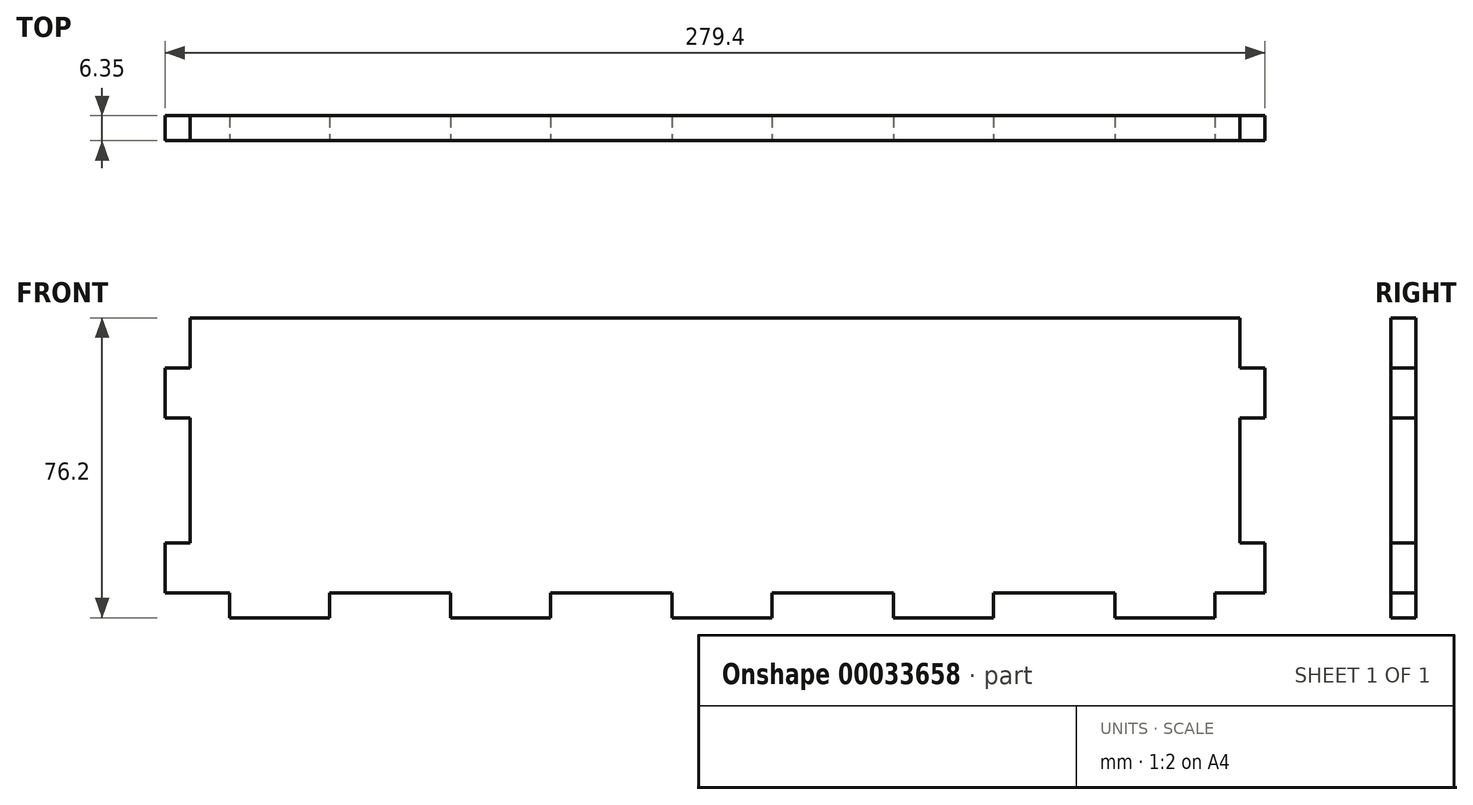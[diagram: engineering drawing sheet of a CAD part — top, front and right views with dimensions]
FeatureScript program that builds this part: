
annotation { "Feature Type Name" : "Feature", "Feature Type Description" : "" }
export const myFeature = defineFeature(function(context is Context, id is Id, definition is map)
    precondition{}
    {
        {
            var Q0;
            Q0=qCreatedBy(makeId("Front.planeOp"),FACE);
            var sketch = newSketch(context, id + "F0", { "sketchPlane" : qUnion([Q0])});
            skLineSegment(sketch, "E0.bottom", {"start": v(0, 0) * mm, "end": v(444.5, 0) * mm});
            skLineSegment(sketch, "E0.top", {"start": v(0, 76.2) * mm, "end": v(444.5, 76.2) * mm});
            skLineSegment(sketch, "E0.left", {"start": v(0, 0) * mm, "end": v(0, 76.2) * mm});
            skLineSegment(sketch, "E0.right", {"start": v(444.5, 0) * mm, "end": v(444.5, 76.2) * mm});
            skSolve(sketch);
        }
        {
            var Q0;
            Q0=makeQuery(id+"F0.imprint","IMPRINT",FACE,{"disambiguationData":[TD([[makeQuery(id+"F0.imprint","IMPRINT",EDGE,{"derivedFrom":sQuery(id+"F0.wireOp",EDGE,"E0.bottom")}),1.0]])]});
            extrude(context, id + "F1", {"entities" : qUnion([Q0]), "depth" : 6.35 * mm});
        }
        {
            var Q0;
            Q0=makeQuery(id+"F1.opExtrude","CAP_FACE",FACE,{"disambiguationData":[OSD([sQuery(id+"F0.wireOp",EDGE,"E0.bottom"),sQuery(id+"F0.wireOp",EDGE,"E0.top"),sQuery(id+"F0.wireOp",EDGE,"E0.left"),sQuery(id+"F0.wireOp",EDGE,"E0.right")])],"isStart":false});
            var sketch = newSketch(context, id + "F2", { "sketchPlane" : qUnion([Q0])});
            skLineSegment(sketch, "E1", {"start": v(222.25, 76.2) * mm, "end": v(222.25, 0) * mm, "construction": true});
            skLineSegment(sketch, "E2.bottom", {"start": v(0, 0) * mm, "end": v(6.35, 0) * mm});
            skLineSegment(sketch, "E2.top", {"start": v(0, 6.35) * mm, "end": v(6.35, 6.35) * mm});
            skLineSegment(sketch, "E2.left", {"start": v(0, 0) * mm, "end": v(0, 6.35) * mm});
            skLineSegment(sketch, "E2.right", {"start": v(6.35, 0) * mm, "end": v(6.35, 6.35) * mm});
            skLineSegment(sketch, "E3.bottom", {"start": v(0, 76.2) * mm, "end": v(6.35, 76.2) * mm});
            skLineSegment(sketch, "E3.top", {"start": v(0, 63.5) * mm, "end": v(6.35, 63.5) * mm});
            skLineSegment(sketch, "E3.left", {"start": v(0, 76.2) * mm, "end": v(0, 63.5) * mm});
            skLineSegment(sketch, "E3.right", {"start": v(6.35, 76.2) * mm, "end": v(6.35, 63.5) * mm});
            skLineSegment(sketch, "E4.bottom", {"start": v(0, 19.05) * mm, "end": v(6.35, 19.05) * mm});
            skLineSegment(sketch, "E4.top", {"start": v(0, 50.8) * mm, "end": v(6.35, 50.8) * mm});
            skLineSegment(sketch, "E4.left", {"start": v(0, 19.05) * mm, "end": v(0, 50.8) * mm});
            skLineSegment(sketch, "E4.right", {"start": v(6.35, 19.05) * mm, "end": v(6.35, 50.8) * mm});
            skLineSegment(sketch, "E5.MirrorCS", {"start": v(444.5, 6.35) * mm, "end": v(438.15, 6.35) * mm});
            skLineSegment(sketch, "E6.MirrorCS", {"start": v(444.5, 19.05) * mm, "end": v(438.15, 19.05) * mm});
            skLineSegment(sketch, "E7.MirrorCS", {"start": v(444.5, 50.8) * mm, "end": v(438.15, 50.8) * mm});
            skLineSegment(sketch, "E8.MirrorCS", {"start": v(444.5, 0) * mm, "end": v(438.15, 0) * mm});
            skLineSegment(sketch, "E9.MirrorCS", {"start": v(438.15, 76.2) * mm, "end": v(438.15, 63.5) * mm});
            skLineSegment(sketch, "E10.MirrorCS", {"start": v(438.15, 0) * mm, "end": v(438.15, 6.35) * mm});
            skLineSegment(sketch, "E11.MirrorCS", {"start": v(444.5, 0) * mm, "end": v(444.5, 6.35) * mm});
            skLineSegment(sketch, "E12.MirrorCS", {"start": v(444.5, 63.5) * mm, "end": v(438.15, 63.5) * mm});
            skLineSegment(sketch, "E13.MirrorCS", {"start": v(444.5, 76.2) * mm, "end": v(438.15, 76.2) * mm});
            skLineSegment(sketch, "E14.MirrorCS", {"start": v(444.5, 76.2) * mm, "end": v(444.5, 63.5) * mm});
            skLineSegment(sketch, "E15.MirrorCS", {"start": v(438.15, 19.05) * mm, "end": v(438.15, 50.8) * mm});
            skLineSegment(sketch, "E16.MirrorCS", {"start": v(444.5, 19.05) * mm, "end": v(444.5, 50.8) * mm});
            skSolve(sketch);
        }
        {
            var Q0;
            Q0=qSketchRegion(id+"F2",true);
            extrude(context, id + "F3", {"entities" : qUnion([Q0]), "operationType" : NewBodyOperationType.REMOVE, "endBound" : BoundingType.UP_TO_NEXT, "oppositeDirection" : true, "depth" : 25.4 * mm});
        }
        {
            var Q0;
            Q0=makeQuery(id+"F1.opExtrude","CAP_FACE",FACE,{"disambiguationData":[OSD([sQuery(id+"F0.wireOp",EDGE,"E0.bottom"),sQuery(id+"F0.wireOp",EDGE,"E0.top"),sQuery(id+"F0.wireOp",EDGE,"E0.left"),sQuery(id+"F0.wireOp",EDGE,"E0.right")])],"isStart":false});
            var sketch = newSketch(context, id + "F4", { "sketchPlane" : qUnion([Q0])});
            skLineSegment(sketch, "E17.bottom", {"start": v(38.1, 0) * mm, "end": v(68.94, 0) * mm});
            skLineSegment(sketch, "E17.top", {"start": v(38.1, 6.35) * mm, "end": v(68.94, 6.35) * mm});
            skLineSegment(sketch, "E17.left", {"start": v(38.1, 0) * mm, "end": v(38.1, 6.35) * mm});
            skLineSegment(sketch, "E17.right", {"start": v(68.94, 0) * mm, "end": v(68.94, 6.35) * mm});
            skLineSegment(sketch, "E18.1.0.0", {"start": v(125.19, 0) * mm, "end": v(125.19, 6.35) * mm});
            skLineSegment(sketch, "E18.1.0.1", {"start": v(94.34, 0) * mm, "end": v(94.34, 6.35) * mm});
            skLineSegment(sketch, "E18.1.0.2", {"start": v(94.34, 6.35) * mm, "end": v(125.19, 6.35) * mm});
            skLineSegment(sketch, "E18.1.0.3", {"start": v(94.34, 0) * mm, "end": v(125.19, 0) * mm});
            skLineSegment(sketch, "E18.2.0.0", {"start": v(181.43, 0) * mm, "end": v(181.43, 6.35) * mm});
            skLineSegment(sketch, "E18.2.0.1", {"start": v(150.59, 0) * mm, "end": v(150.59, 6.35) * mm});
            skLineSegment(sketch, "E18.2.0.2", {"start": v(150.59, 6.35) * mm, "end": v(181.43, 6.35) * mm});
            skLineSegment(sketch, "E18.2.0.3", {"start": v(150.59, 0) * mm, "end": v(181.43, 0) * mm});
            skLineSegment(sketch, "E18.3.0.0", {"start": v(237.67, 0) * mm, "end": v(237.67, 6.35) * mm});
            skLineSegment(sketch, "E18.3.0.1", {"start": v(206.83, 0) * mm, "end": v(206.83, 6.35) * mm});
            skLineSegment(sketch, "E18.3.0.2", {"start": v(206.83, 6.35) * mm, "end": v(237.67, 6.35) * mm});
            skLineSegment(sketch, "E18.3.0.3", {"start": v(206.83, 0) * mm, "end": v(237.67, 0) * mm});
            skLineSegment(sketch, "E18.4.0.0", {"start": v(293.91, 0) * mm, "end": v(293.91, 6.35) * mm});
            skLineSegment(sketch, "E18.4.0.1", {"start": v(263.07, 0) * mm, "end": v(263.07, 6.35) * mm});
            skLineSegment(sketch, "E18.4.0.2", {"start": v(263.07, 6.35) * mm, "end": v(293.91, 6.35) * mm});
            skLineSegment(sketch, "E18.4.0.3", {"start": v(263.07, 0) * mm, "end": v(293.91, 0) * mm});
            skLineSegment(sketch, "E18.direction1", {"start": v(68.94, 0) * mm, "end": v(125.19, 0) * mm, "construction": true});
            skLineSegment(sketch, "E19.0.5.0", {"start": v(350.16, 0) * mm, "end": v(350.16, 6.35) * mm});
            skLineSegment(sketch, "E19.3.5.0", {"start": v(319.31, 0) * mm, "end": v(319.31, 6.35) * mm});
            skLineSegment(sketch, "E19.6.5.0", {"start": v(319.31, 6.35) * mm, "end": v(350.16, 6.35) * mm});
            skLineSegment(sketch, "E19.9.5.0", {"start": v(319.31, 0) * mm, "end": v(350.16, 0) * mm});
            skLineSegment(sketch, "E19.0.6.0", {"start": v(406.4, 0) * mm, "end": v(406.4, 6.35) * mm});
            skLineSegment(sketch, "E19.3.6.0", {"start": v(375.56, 0) * mm, "end": v(375.56, 6.35) * mm});
            skLineSegment(sketch, "E19.6.6.0", {"start": v(375.56, 6.35) * mm, "end": v(406.4, 6.35) * mm});
            skLineSegment(sketch, "E19.9.6.0", {"start": v(375.56, 0) * mm, "end": v(406.4, 0) * mm});
            skLineSegment(sketch, "E20.bottom", {"start": v(6.35, 6.35) * mm, "end": v(12.7, 6.35) * mm});
            skLineSegment(sketch, "E20.top", {"start": v(6.35, 0) * mm, "end": v(12.7, 0) * mm});
            skLineSegment(sketch, "E20.left", {"start": v(6.35, 6.35) * mm, "end": v(6.35, 0) * mm});
            skLineSegment(sketch, "E20.right", {"start": v(12.7, 6.35) * mm, "end": v(12.7, 0) * mm});
            skLineSegment(sketch, "E21.bottom", {"start": v(438.15, 6.35) * mm, "end": v(431.8, 6.35) * mm});
            skLineSegment(sketch, "E21.top", {"start": v(438.15, 0) * mm, "end": v(431.8, 0) * mm});
            skLineSegment(sketch, "E21.left", {"start": v(438.15, 6.35) * mm, "end": v(438.15, 0) * mm});
            skLineSegment(sketch, "E21.right", {"start": v(431.8, 6.35) * mm, "end": v(431.8, 0) * mm});
            skSolve(sketch);
        }
        {
            var Q0;
            Q0=qSketchRegion(id+"F4",true);
            extrude(context, id + "F5", {"entities" : qUnion([Q0]), "operationType" : NewBodyOperationType.REMOVE, "endBound" : BoundingType.THROUGH_ALL, "oppositeDirection" : true, "depth" : 25.4 * mm});
        }
        {
            var Q0;
            Q0=makeQuery(id+"F1.opExtrude","CAP_FACE",FACE,{"disambiguationData":[OSD([sQuery(id+"F0.wireOp",EDGE,"E0.bottom"),sQuery(id+"F0.wireOp",EDGE,"E0.top"),sQuery(id+"F0.wireOp",EDGE,"E0.left"),sQuery(id+"F0.wireOp",EDGE,"E0.right")])],"isStart":false});
            var sketch = newSketch(context, id + "F6", { "sketchPlane" : qUnion([Q0])});
            skLineSegment(sketch, "E22.bottom", {"start": v(165.1, 76.2) * mm, "end": v(0, 76.2) * mm});
            skLineSegment(sketch, "E22.top", {"start": v(165.1, 0) * mm, "end": v(0, 0) * mm});
            skLineSegment(sketch, "E22.left", {"start": v(165.1, 76.2) * mm, "end": v(165.1, 0) * mm});
            skLineSegment(sketch, "E22.right", {"start": v(0, 76.2) * mm, "end": v(0, 0) * mm});
            skSolve(sketch);
        }
        {
            var Q0;
            Q0 = qSketchRegion(id + "F6", true);
            extrude(context, id + "F7", {"entities" : qUnion([Q0]), "operationType" : NewBodyOperationType.REMOVE, "endBound" : BoundingType.THROUGH_ALL, "oppositeDirection" : true, "depth" : 25.4 * mm});
        }
        {
            var Q0;
            Q0=makeQuery(id+"F1.opExtrude","CAP_FACE",FACE,{"disambiguationData":[OSD([sQuery(id+"F0.wireOp",EDGE,"E0.bottom"),sQuery(id+"F0.wireOp",EDGE,"E0.top"),sQuery(id+"F0.wireOp",EDGE,"E0.left"),sQuery(id+"F0.wireOp",EDGE,"E0.right")])],"isStart":false});
            var sketch = newSketch(context, id + "F8", { "sketchPlane" : qUnion([Q0])});
            skLineSegment(sketch, "E23.0", {"start": v(438.15, 19.05) * mm, "end": v(438.15, 50.8) * mm, "construction": true});
            skLineSegment(sketch, "E24.0", {"start": v(438.15, 76.2) * mm, "end": v(438.15, 63.5) * mm, "construction": true});
            skLineSegment(sketch, "E25.0", {"start": v(444.5, 50.8) * mm, "end": v(438.15, 50.8) * mm, "construction": true});
            skLineSegment(sketch, "E26.0", {"start": v(444.5, 19.05) * mm, "end": v(438.15, 19.05) * mm, "construction": true});
            skLineSegment(sketch, "E27.0", {"start": v(444.5, 63.5) * mm, "end": v(438.15, 63.5) * mm, "construction": true});
            skLineSegment(sketch, "E28", {"start": v(438.15, 76.2) * mm, "end": v(444.5, 76.2) * mm, "construction": true});
            skLineSegment(sketch, "E29", {"start": v(444.5, 63.5) * mm, "end": v(444.5, 76.2) * mm});
            skLineSegment(sketch, "E30", {"start": v(304.8, 76.2) * mm, "end": v(304.8, 0) * mm, "construction": true});
            skLineSegment(sketch, "E31", {"start": v(444.5, 19.05) * mm, "end": v(444.5, 50.8) * mm, "construction": true});
            skLineSegment(sketch, "E32.MirrorCS", {"start": v(171.45, 76.2) * mm, "end": v(165.1, 76.2) * mm});
            skLineSegment(sketch, "E33.MirrorCS", {"start": v(165.1, 63.5) * mm, "end": v(171.45, 63.5) * mm});
            skLineSegment(sketch, "E34.MirrorCS", {"start": v(165.1, 50.8) * mm, "end": v(171.45, 50.8) * mm});
            skLineSegment(sketch, "E35.MirrorCS", {"start": v(165.1, 19.05) * mm, "end": v(171.45, 19.05) * mm});
            skLineSegment(sketch, "E36.MirrorCS", {"start": v(165.1, 63.5) * mm, "end": v(165.1, 76.2) * mm});
            skLineSegment(sketch, "E37.MirrorCS", {"start": v(165.1, 19.05) * mm, "end": v(165.1, 50.8) * mm});
            skLineSegment(sketch, "E38.MirrorCS", {"start": v(171.45, 76.2) * mm, "end": v(171.45, 63.5) * mm});
            skLineSegment(sketch, "E39.MirrorCS", {"start": v(171.45, 19.05) * mm, "end": v(171.45, 50.8) * mm});
            skSolve(sketch);
        }
        {
            var Q0;
            Q0 = qSketchRegion(id + "F8", true);
            extrude(context, id + "F9", {"entities" : qUnion([Q0]), "operationType" : NewBodyOperationType.REMOVE, "endBound" : BoundingType.THROUGH_ALL, "oppositeDirection" : true, "depth" : 25.4 * mm});
        }
    });
